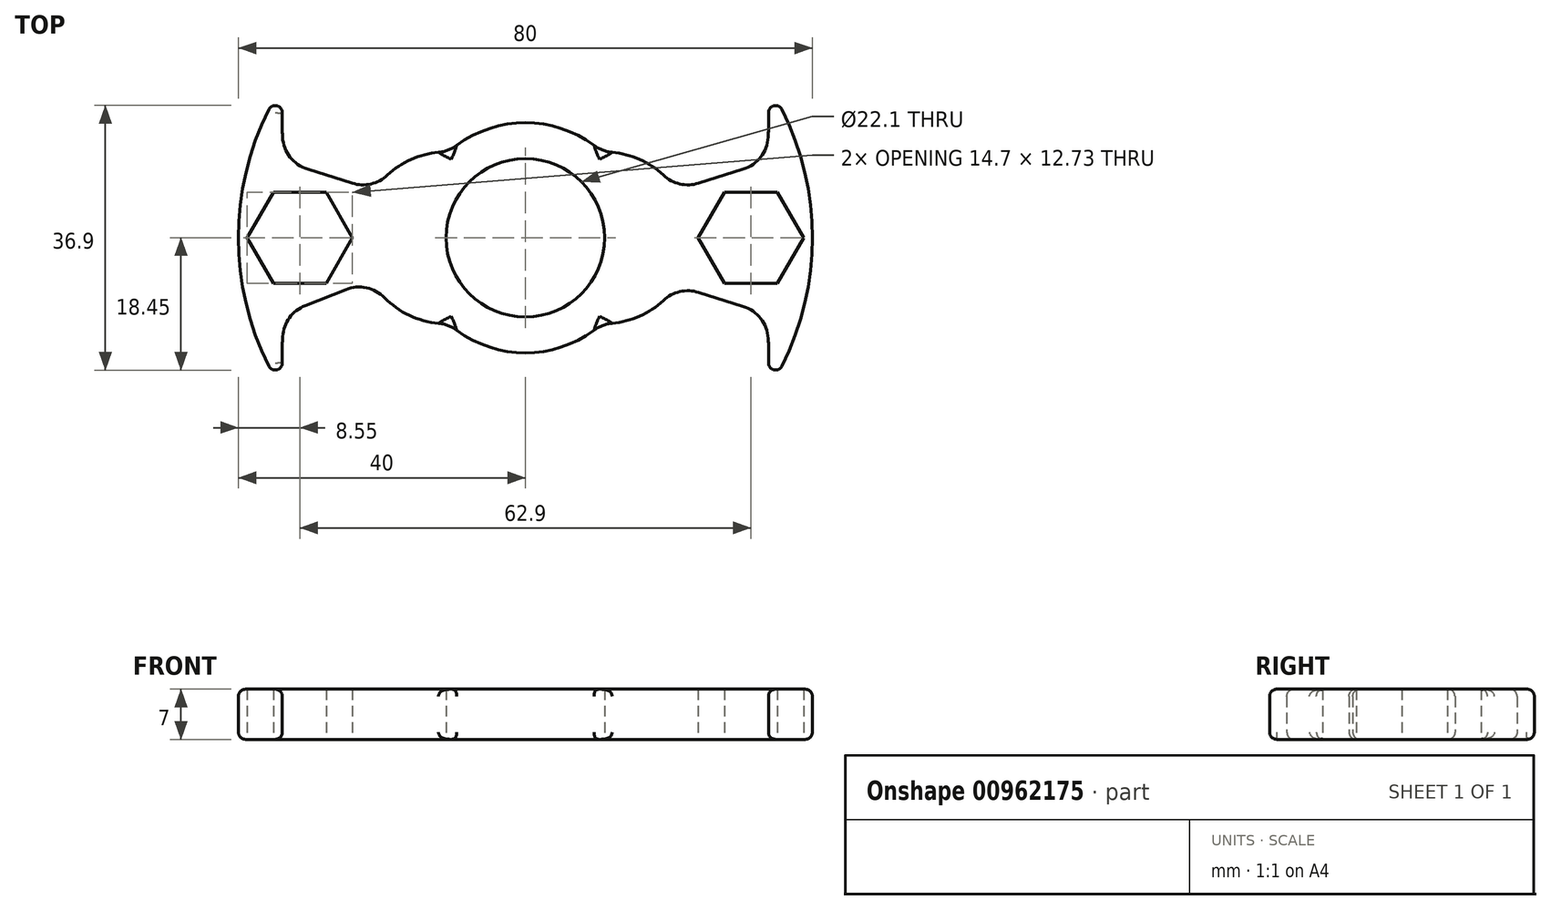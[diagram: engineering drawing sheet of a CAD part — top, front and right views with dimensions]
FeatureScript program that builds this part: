
annotation { "Feature Type Name" : "Feature", "Feature Type Description" : "" }
export const myFeature = defineFeature(function(context is Context, id is Id, definition is map)
    precondition{}
    {
        {
            var Q0;
            Q0=qCreatedBy(makeId("Top.planeOp"),FACE);
            var sketch = newSketch(context, id + "F0", { "sketchPlane" : qUnion([Q0])});
            skCircle(sketch, "E0", {"center": v(0, 0) * mm, "radius": 11.05 * mm});
            skArc(sketch, "E1.0", {"start": v(-10.7, -11.96) * mm, "mid": v(0, -16.05) * mm, "end": v(10.7, -11.96) * mm});
            skLineSegment(sketch, "E2", {"start": v(-30.36, 9.57) * mm, "end": v(-26.73, 8.43) * mm});
            skLineSegment(sketch, "E3", {"start": v(30.36, 9.57) * mm, "end": v(24.15, 7.62) * mm});
            skArc(sketch, "E4", {"start": v(-38.15, 12.03) * mm, "mid": v(-40, 0) * mm, "end": v(-38.15, -12.03) * mm});
            skArc(sketch, "E5", {"start": v(38.15, 12.03) * mm, "mid": v(40, 0) * mm, "end": v(38.15, -12.03) * mm});
            skLineSegment(sketch, "E6", {"start": v(24.15, -7.62) * mm, "end": v(26.73, -8.43) * mm});
            skLineSegment(sketch, "E7", {"start": v(-26.73, 8.43) * mm, "end": v(-24.15, 7.62) * mm});
            skLineSegment(sketch, "E8", {"start": v(26.73, -8.43) * mm, "end": v(30.36, -9.57) * mm});
            skArc(sketch, "E9", {"start": v(-19.23, 8.74) * mm, "mid": v(-15.29, 11.2) * mm, "end": v(-10.7, 11.96) * mm});
            skArc(sketch, "E10", {"start": v(19.23, -8.74) * mm, "mid": v(15.29, -11.2) * mm, "end": v(10.7, -11.96) * mm});
            skArc(sketch, "E11", {"start": v(19.23, 8.74) * mm, "mid": v(15.29, 11.2) * mm, "end": v(10.7, 11.96) * mm});
            skArc(sketch, "E12", {"start": v(-19.61, -8.36) * mm, "mid": v(-15.53, -11.1) * mm, "end": v(-10.7, -11.96) * mm});
            skArc(sketch, "E13", {"start": v(-38.15, 12.03) * mm, "mid": v(-36.11, 17.2) * mm, "end": v(-33.37, 22.05) * mm});
            skArc(sketch, "E14", {"start": v(38.15, -12.03) * mm, "mid": v(36.11, -17.2) * mm, "end": v(33.37, -22.05) * mm});
            skArc(sketch, "E15", {"start": v(40, 0) * mm, "mid": v(38.3, 11.51) * mm, "end": v(33.37, 22.05) * mm});
            skArc(sketch, "E16", {"start": v(-38.15, -12.03) * mm, "mid": v(-36.11, -17.2) * mm, "end": v(-33.37, -22.05) * mm});
            skArc(sketch, "E17", {"start": v(33.37, 22.05) * mm, "mid": v(33.85, 18.06) * mm, "end": v(33.85, 14.05) * mm});
            skArc(sketch, "E18", {"start": v(-33.37, 22.05) * mm, "mid": v(-33.85, 18.06) * mm, "end": v(-33.85, 14.05) * mm});
            skArc(sketch, "E19", {"start": v(33.37, -22.05) * mm, "mid": v(33.85, -18.06) * mm, "end": v(33.85, -14.05) * mm});
            skArc(sketch, "E20", {"start": v(-33.37, -22.05) * mm, "mid": v(-33.86, -17.92) * mm, "end": v(-33.83, -13.76) * mm});
            skCircle(sketch, "E21.cCircle", {"center": v(-31.45, 0) * mm, "radius": 7.35 * mm, "construction": true});
            skLineSegment(sketch, "E21.0", {"start": v(-24.1, 0) * mm, "end": v(-27.78, -6.37) * mm});
            skLineSegment(sketch, "E21.1", {"start": v(-27.78, -6.37) * mm, "end": v(-35.12, -6.37) * mm});
            skLineSegment(sketch, "E21.2", {"start": v(-35.12, -6.37) * mm, "end": v(-38.8, 0) * mm});
            skLineSegment(sketch, "E21.3", {"start": v(-38.8, 0) * mm, "end": v(-35.12, 6.37) * mm});
            skLineSegment(sketch, "E21.4", {"start": v(-35.12, 6.37) * mm, "end": v(-27.78, 6.37) * mm});
            skLineSegment(sketch, "E21.5", {"start": v(-27.78, 6.37) * mm, "end": v(-24.1, 0) * mm});
            skCircle(sketch, "E22.cCircle", {"center": v(31.45, 0) * mm, "radius": 7.35 * mm, "construction": true});
            skLineSegment(sketch, "E22.0", {"start": v(38.8, 0) * mm, "end": v(35.12, -6.37) * mm});
            skLineSegment(sketch, "E22.1", {"start": v(35.12, -6.37) * mm, "end": v(27.78, -6.37) * mm});
            skLineSegment(sketch, "E22.2", {"start": v(27.78, -6.37) * mm, "end": v(24.1, 0) * mm});
            skLineSegment(sketch, "E22.3", {"start": v(24.1, 0) * mm, "end": v(27.78, 6.37) * mm});
            skLineSegment(sketch, "E22.4", {"start": v(27.78, 6.37) * mm, "end": v(35.12, 6.37) * mm});
            skLineSegment(sketch, "E22.5", {"start": v(35.12, 6.37) * mm, "end": v(38.8, 0) * mm});
            skPoint(sketch, "E23.newPointB", {"position": v(-38.15, -12.03) * mm});
            skArc(sketch, "E23.filletArc", {"start": v(19.23, 8.74) * mm, "mid": v(21.54, 7.5) * mm, "end": v(24.15, 7.62) * mm});
            skPoint(sketch, "E24.newPointA", {"position": v(15.3, -4.83) * mm});
            skPoint(sketch, "E24.newPointB", {"position": v(21.02, -6.63) * mm});
            skArc(sketch, "E24.filletArc", {"start": v(24.15, -7.62) * mm, "mid": v(21.54, -7.5) * mm, "end": v(19.23, -8.74) * mm});
            skPoint(sketch, "E25.newPointA", {"position": v(-15.3, 4.83) * mm});
            skPoint(sketch, "E25.newPointB", {"position": v(-21.02, 6.63) * mm});
            skArc(sketch, "E25.filletArc", {"start": v(-24.15, 7.62) * mm, "mid": v(-21.54, 7.5) * mm, "end": v(-19.23, 8.74) * mm});
            skLineSegment(sketch, "E26", {"start": v(-30.69, -9.45) * mm, "end": v(-25.04, -7.2) * mm});
            skArc(sketch, "E27.filletArc", {"start": v(-19.61, -8.36) * mm, "mid": v(-22.15, -6.96) * mm, "end": v(-25.04, -7.2) * mm});
            skPoint(sketch, "E28.orphan", {"position": v(38.15, -12.03) * mm});
            skArc(sketch, "E29.trimOffspring", {"start": v(10.7, 11.96) * mm, "mid": v(0, 16.05) * mm, "end": v(-10.7, 11.96) * mm});
            skPoint(sketch, "E30.visualSharp", {"position": v(-33.46, 10.55) * mm});
            skArc(sketch, "E30.filletArc", {"start": v(-33.85, 14.05) * mm, "mid": v(-32.8, 11.27) * mm, "end": v(-30.36, 9.57) * mm});
            skPoint(sketch, "E31.visualSharp", {"position": v(-33.46, -10.55) * mm});
            skArc(sketch, "E31.filletArc", {"start": v(-30.69, -9.45) * mm, "mid": v(-32.88, -11.15) * mm, "end": v(-33.83, -13.76) * mm});
            skPoint(sketch, "E32.visualSharp", {"position": v(33.46, -10.55) * mm});
            skArc(sketch, "E32.filletArc", {"start": v(33.85, -14.05) * mm, "mid": v(32.8, -11.27) * mm, "end": v(30.36, -9.57) * mm});
            skPoint(sketch, "E33.visualSharp", {"position": v(33.46, 10.55) * mm});
            skArc(sketch, "E33.filletArc", {"start": v(30.36, 9.57) * mm, "mid": v(32.8, 11.27) * mm, "end": v(33.85, 14.05) * mm});
            skSolve(sketch);
        }
        {
            var Q0;
            Q0 = qSketchRegion(id + "F0", true);
            extrude(context, id + "F1", {"entities" : qUnion([Q0]), "depth" : 7 * mm, "offsetDistance" : 25 * mm});
        }
        {
            var Q0;
            Q0=makeQuery(id+"F1.opExtrude","SWEPT_EDGE",EDGE,{"disambiguationData":[OSD([sQuery(id+"F0.wireOp",EDGE,"E16"),sQuery(id+"F0.wireOp",EDGE,"E20")])]});
            var Q1;
            Q1=makeQuery(id+"F1.opExtrude","SWEPT_EDGE",EDGE,{"disambiguationData":[OSD([sQuery(id+"F0.wireOp",EDGE,"E14"),sQuery(id+"F0.wireOp",EDGE,"E19")])]});
            var Q2;
            Q2=makeQuery(id+"F1.opExtrude","SWEPT_EDGE",EDGE,{"disambiguationData":[OSD([sQuery(id+"F0.wireOp",EDGE,"E15"),sQuery(id+"F0.wireOp",EDGE,"E17")])]});
            var Q3;
            Q3=makeQuery(id+"F1.opExtrude","SWEPT_EDGE",EDGE,{"disambiguationData":[OSD([sQuery(id+"F0.wireOp",EDGE,"E13"),sQuery(id+"F0.wireOp",EDGE,"E18")])]});
            var Q4;
            Q4=makeQuery(id+"F1.opExtrude","CAP_EDGE",EDGE,{"disambiguationData":[OSD([sQuery(id+"F0.wireOp",EDGE,"E29.trimOffspring")])],"isStart":false});
            var Q5;
            Q5=makeQuery(id+"F1.opExtrude","CAP_EDGE",EDGE,{"disambiguationData":[OSD([sQuery(id+"F0.wireOp",EDGE,"E9")])],"isStart":false});
            var Q6;
            Q6=makeQuery(id+"F1.opExtrude","CAP_EDGE",EDGE,{"disambiguationData":[OSD([sQuery(id+"F0.wireOp",EDGE,"E11")])],"isStart":false});
            var Q7;
            Q7=makeQuery(id+"F1.opExtrude","CAP_EDGE",EDGE,{"disambiguationData":[OSD([sQuery(id+"F0.wireOp",EDGE,"E5"),sQuery(id+"F0.wireOp",EDGE,"E14"),sQuery(id+"F0.wireOp",EDGE,"E15")])],"isStart":false});
            var Q8;
            Q8=makeQuery(id+"F1.opExtrude","CAP_EDGE",EDGE,{"disambiguationData":[OSD([sQuery(id+"F0.wireOp",EDGE,"E10")])],"isStart":false});
            var Q9;
            Q9=makeQuery(id+"F1.opExtrude","CAP_EDGE",EDGE,{"disambiguationData":[OSD([sQuery(id+"F0.wireOp",EDGE,"E1.0")])],"isStart":false});
            var Q10;
            Q10=makeQuery(id+"F1.opExtrude","CAP_EDGE",EDGE,{"disambiguationData":[OSD([sQuery(id+"F0.wireOp",EDGE,"E12")])],"isStart":false});
            var Q11;
            Q11=makeQuery(id+"F1.opExtrude","CAP_EDGE",EDGE,{"disambiguationData":[OSD([sQuery(id+"F0.wireOp",EDGE,"E4"),sQuery(id+"F0.wireOp",EDGE,"E13"),sQuery(id+"F0.wireOp",EDGE,"E16")])],"isStart":false});
            fillet(context, id + "F2", {"entities" : qUnion([Q0, Q1, Q2, Q3, Q4, Q5, Q6, Q7, Q8, Q9, Q10, Q11]), "radius" : 1 * mm, "tangentPropagation" : true, "allowEdgeOverflow" : false});
        }
        {
            var Q0;
            Q0=makeQuery(id+"F1.opExtrude","CAP_EDGE",EDGE,{"disambiguationData":[OSD([sQuery(id+"F0.wireOp",EDGE,"E1.0")])],"isStart":true});
            var Q1;
            Q1=makeQuery(id+"F1.opExtrude","CAP_EDGE",EDGE,{"disambiguationData":[OSD([sQuery(id+"F0.wireOp",EDGE,"E12")])],"isStart":true});
            var Q2;
            Q2=makeQuery(id+"F1.opExtrude","CAP_EDGE",EDGE,{"disambiguationData":[OSD([sQuery(id+"F0.wireOp",EDGE,"E10")])],"isStart":true});
            var Q3;
            Q3=makeQuery(id+"F1.opExtrude","CAP_EDGE",EDGE,{"disambiguationData":[OSD([sQuery(id+"F0.wireOp",EDGE,"E29.trimOffspring")])],"isStart":true});
            fillet(context, id + "F3", {"entities" : qUnion([Q0, Q1, Q2, Q3]), "radius" : 1 * mm, "tangentPropagation" : true, "allowEdgeOverflow" : false});
        }
        {
            var Q0;
            Q0=makeQuery(id+"F1.opExtrude","SWEPT_EDGE",EDGE,{"disambiguationData":[OSD([sQuery(id+"F0.wireOp",EDGE,"E9"),sQuery(id+"F0.wireOp",EDGE,"E29.trimOffspring")])]});
            var Q1;
            Q1=makeQuery(id+"F1.opExtrude","SWEPT_EDGE",EDGE,{"disambiguationData":[OSD([sQuery(id+"F0.wireOp",EDGE,"E11"),sQuery(id+"F0.wireOp",EDGE,"E29.trimOffspring")])]});
            var Q2;
            Q2=makeQuery(id+"F1.opExtrude","SWEPT_EDGE",EDGE,{"disambiguationData":[OSD([sQuery(id+"F0.wireOp",EDGE,"E1.0"),sQuery(id+"F0.wireOp",EDGE,"E10")])]});
            var Q3;
            Q3=makeQuery(id+"F1.opExtrude","SWEPT_EDGE",EDGE,{"disambiguationData":[OSD([sQuery(id+"F0.wireOp",EDGE,"E1.0"),sQuery(id+"F0.wireOp",EDGE,"E12")])]});
            fillet(context, id + "F4", {"entities" : qUnion([Q0, Q1, Q2, Q3]), "radius" : 5 * mm, "tangentPropagation" : true, "allowEdgeOverflow" : false});
        }
    });
